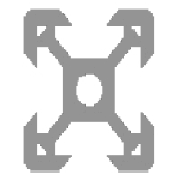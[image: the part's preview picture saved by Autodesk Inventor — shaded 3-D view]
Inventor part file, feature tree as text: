
AUTODESK INVENTOR PART (.ipt)
format: ipt  version: 2013 (Build 170138000, 138)  size: 192,512 bytes
history: native  units: mm
features: other x4, plane x2, sketch x2, split x1
ambient origin geometry x8: Origin, YZ Plane, XZ Plane, XY Plane, X Axis, Y Axis, Z Axis, Center Point
bodies: Solid1 (feature_tree), Body (feature_tree)
feature tree (9):
  other  "Driven Length"
  other  "Frame Generator"
  other  "Start Plane"
  other  "End Plane"
  plane  "Work Plane5"
  split  "Split1"
  sketch  "Sketch4"  dims[d2=4.2mm]
  plane  "Work Plane4"
  sketch  "Sketch5"  dims[d3=1.5mm d4=1.64mm d5=1.8mm d6=5.68mm d7=1.8mm d9=1.5mm d12=-0.0mm d13=195.0mm d14=0.13mm d15=0.0mm d18=90.0deg d17=195.0mm]
